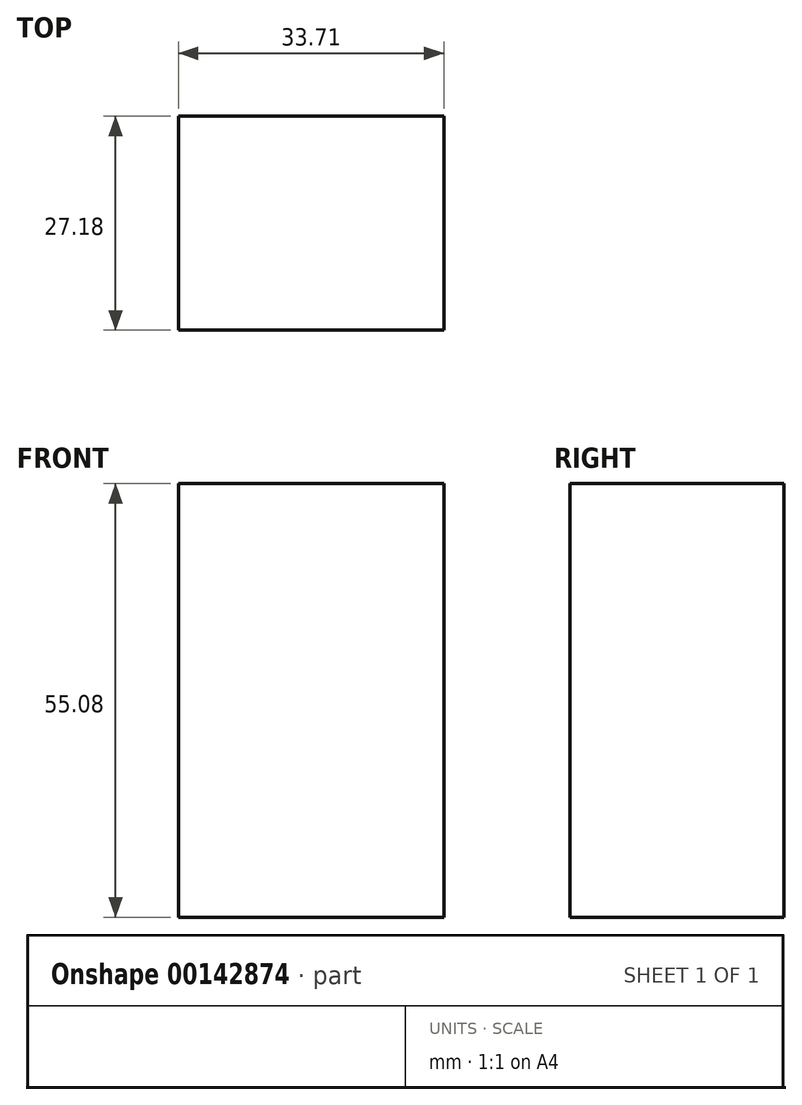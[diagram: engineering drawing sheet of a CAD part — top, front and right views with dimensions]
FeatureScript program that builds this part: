
annotation { "Feature Type Name" : "Feature", "Feature Type Description" : "" }
export const myFeature = defineFeature(function(context is Context, id is Id, definition is map)
    precondition{}
    {
        {
            var Q0;
            Q0=qCreatedBy(makeId("Top.planeOp"),FACE);
            var sketch = newSketch(context, id + "F0", { "sketchPlane" : qUnion([Q0])});
            skLineSegment(sketch, "E0.bottom", {"start": v(-76.04, -24.82) * mm, "end": v(-42.33, -24.82) * mm});
            skLineSegment(sketch, "E0.top", {"start": v(-76.04, -52) * mm, "end": v(-42.33, -52) * mm});
            skLineSegment(sketch, "E0.left", {"start": v(-76.04, -24.82) * mm, "end": v(-76.04, -52) * mm});
            skLineSegment(sketch, "E0.right", {"start": v(-42.33, -24.82) * mm, "end": v(-42.33, -52) * mm});
            skSolve(sketch);
        }
        {
            var Q0;
            Q0=makeQuery(id+"F0.imprint","IMPRINT",FACE,{"disambiguationData":[TD([[makeQuery(id+"F0.imprint","IMPRINT",EDGE,{"derivedFrom":sQuery(id+"F0.wireOp",EDGE,"E0.bottom")}),-1.0]])]});
            extrude(context, id + "F1", {"entities" : qUnion([Q0]), "depth" : 55.08 * mm});
        }
    });
